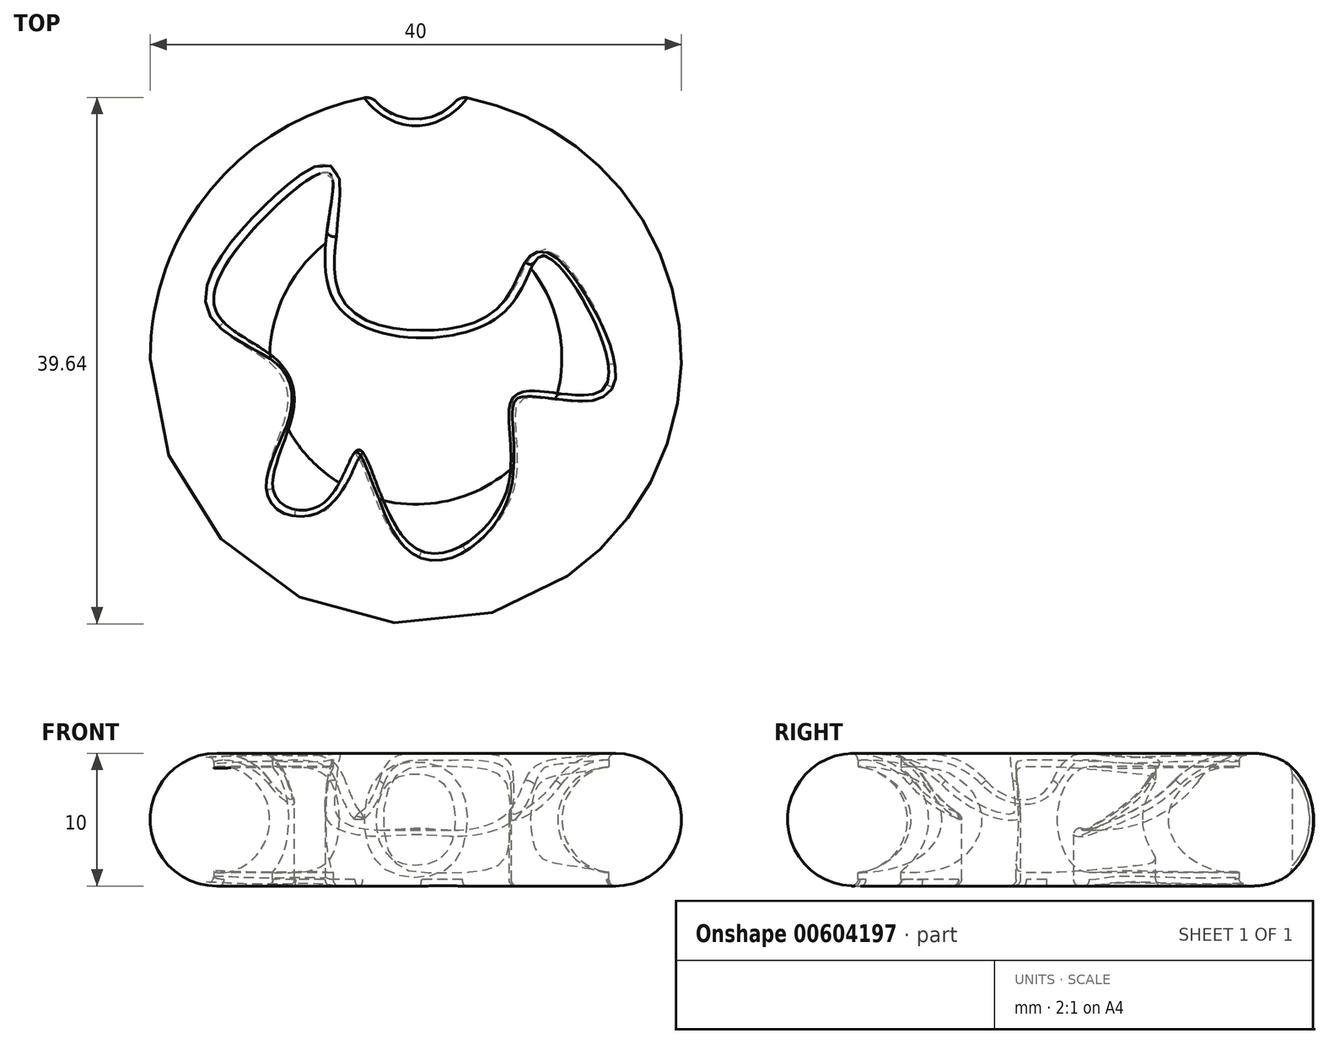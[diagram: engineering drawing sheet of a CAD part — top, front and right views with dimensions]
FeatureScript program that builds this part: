
annotation { "Feature Type Name" : "Feature", "Feature Type Description" : "" }
export const myFeature = defineFeature(function(context is Context, id is Id, definition is map)
    precondition{}
    {
        {
            var Q0;
            Q0=qCreatedBy(makeId("Front.planeOp"),FACE);
            var sketch = newSketch(context, id + "F0", { "sketchPlane" : qUnion([Q0])});
            skArc(sketch, "E0", {"start": v(-10.95, 7.94) * mm, "mid": v(-6, 4.53) * mm, "end": v(0, 5) * mm});
            skArc(sketch, "E1", {"start": v(-10.95, 7.94) * mm, "mid": v(-19.45, 7.27) * mm, "end": v(-15, 0) * mm});
            skLineSegment(sketch, "E2", {"start": v(-15, 0) * mm, "end": v(0, 0) * mm});
            skLineSegment(sketch, "E3", {"start": v(0, 0) * mm, "end": v(0, 5) * mm});
            skPoint(sketch, "E4.orphan", {"position": v(-17.04, 0) * mm});
            skSolve(sketch);
        }
        {
            var Q0;
            Q0=makeQuery(id+"F0.imprint","IMPRINT",FACE,{"disambiguationData":[TD([[makeQuery(id+"F0.imprint","IMPRINT",EDGE,{"derivedFrom":sQuery(id+"F0.wireOp",EDGE,"E0")}),-1.0]])]});
            var Q1;
            Q1=sQuery(id+"F0.wireOp",EDGE,"E3");
            revolve(context, id + "F1", {"entities" : qUnion([Q0]), "axis" : qUnion([Q1]), "revolveType" : RevolveType.FULL});
        }
        {
            var Q0;
            Q0=qCreatedBy(makeId("Top.planeOp"),FACE);
            cPlane(context, id + "F2", {"entities" : qUnion([Q0]), "cplaneType" : CPlaneType.OFFSET, "offset" : 10 * mm, "width" : 150 * mm, "height" : 150 * mm});
        }
        {
            var Q0;
            Q0=qCreatedBy(id+"F2.planeOp",FACE);
            var sketch = newSketch(context, id + "F3", { "sketchPlane" : qUnion([Q0])});
            skFitSpline(sketch, "E5", {"points": [v(-15.11, 3.71) * mm, v(-11.13, 10.87) * mm, v(-6.36, 13.79) * mm, v(-6.1, 4.24) * mm, v(6.63, 3.45) * mm, v(9.8, 7.69) * mm, v(14.32, -2.12) * mm, v(7.69, -2.65) * mm, v(6.9, -9.8) * mm, v(0, -14.32) * mm, v(-4.24, -6.9) * mm, v(-6.9, -10.87) * mm, v(-10.6, -10.34) * mm, v(-9.28, -4.24) * mm, v(-10.6, 0) * mm, v(-15.11, 3.71) * mm]});
            skSolve(sketch);
        }
        {
            var Q0;
            Q0=qSketchRegion(id+"F3",true);
            extrude(context, id + "F4", {"entities" : qUnion([Q0]), "operationType" : NewBodyOperationType.REMOVE, "endBound" : BoundingType.THROUGH_ALL, "oppositeDirection" : true, "depth" : 25 * mm});
        }
        {
            var Q0;
            Q0=qCreatedBy(makeId("Front.planeOp"),FACE);
            var sketch = newSketch(context, id + "F5", { "sketchPlane" : qUnion([Q0])});
            skCircle(sketch, "E6", {"center": v(-15, 5) * mm, "radius": 4 * mm});
            skSolve(sketch);
        }
        {
            var Q0;
            Q0=qSketchRegion(id+"F5",true);
            var Q1;
            Q1=sQuery(id+"F0.wireOp",EDGE,"E3");
            revolve(context, id + "F6", {"operationType" : NewBodyOperationType.ADD, "entities" : qUnion([Q0]), "axis" : qUnion([Q1]), "revolveType" : RevolveType.FULL});
        }
        {
            var Q0;
            Q0=qCreatedBy(makeId("Top.planeOp"),FACE);
            var sketch = newSketch(context, id + "F7", { "sketchPlane" : qUnion([Q0])});
            skCircle(sketch, "E7", {"center": v(0, 22) * mm, "radius": 4 * mm});
            skSolve(sketch);
        }
        {
            var Q0;
            Q0=makeQuery(id+"F7.imprint","IMPRINT",FACE,{"disambiguationData":[TD([[makeQuery(id+"F7.imprint","IMPRINT",EDGE,{"derivedFrom":sQuery(id+"F7.wireOp",EDGE,"E7")}),1.0]])]});
            extrude(context, id + "F8", {"entities" : qUnion([Q0]), "operationType" : NewBodyOperationType.REMOVE, "oppositeDirection" : true, "depth" : 25 * mm});
        }
        {
            var Q0;
            Q0=makeQuery(id+"F7.imprint","IMPRINT",FACE,{"disambiguationData":[TD([[makeQuery(id+"F7.imprint","IMPRINT",EDGE,{"derivedFrom":sQuery(id+"F7.wireOp",EDGE,"E7")}),1.0]])]});
            extrude(context, id + "F9", {"entities" : qUnion([Q0]), "operationType" : NewBodyOperationType.REMOVE, "oppositeDirection" : true, "depth" : 25 * mm});
        }
        {
            var Q0;
            Q0=makeQuery(id+"F7.imprint","IMPRINT",FACE,{"disambiguationData":[TD([[makeQuery(id+"F7.imprint","IMPRINT",EDGE,{"derivedFrom":sQuery(id+"F7.wireOp",EDGE,"E7")}),1.0]])]});
            extrude(context, id + "F10", {"entities" : qUnion([Q0]), "operationType" : NewBodyOperationType.REMOVE, "depth" : 34.3 * mm});
        }
        {
            var Q0;
            Q0=makeQuery(id+"F10.boolean.opBoolean","INTERSECT",EDGE,{"derivedFrom":[makeQuery(id+"F1.opRevolve","SWEPT_FACE",FACE,{"disambiguationData":[OSD([sQuery(id+"F0.wireOp",EDGE,"E1")])]}),makeQuery(id+"F10.opExtrude","SWEPT_FACE",FACE,{"disambiguationData":[OSD([sQuery(id+"F7.wireOp",EDGE,"E7")])]})]});
            fillet(context, id + "F11", {"entities" : qUnion([Q0]), "radius" : 1 * mm, "tangentPropagation" : true, "allowEdgeOverflow" : false});
        }
        {
            var Q0;
            Q0=makeQuery(id+"F4.boolean.opBoolean","INTERSECT",EDGE,{"derivedFrom":[makeQuery(id+"F1.opRevolve","SWEPT_FACE",FACE,{"disambiguationData":[OSD([sQuery(id+"F0.wireOp",EDGE,"E2")])]}),makeQuery(id+"F4.opExtrude","SWEPT_FACE",FACE,{"disambiguationData":[OSD([sQuery(id+"F3.wireOp",EDGE,"E5")])]})]});
            var Q1;
            Q1=makeQuery(id+"F4.boolean.opBoolean","INTERSECT",EDGE,{"disambiguationData":[OD(1.0)],"derivedFrom":[makeQuery(id+"F1.opRevolve","SWEPT_FACE",FACE,{"disambiguationData":[OSD([sQuery(id+"F0.wireOp",EDGE,"E1")])]}),makeQuery(id+"F4.opExtrude","SWEPT_FACE",FACE,{"disambiguationData":[OSD([sQuery(id+"F3.wireOp",EDGE,"E5")])]})]});
            fillet(context, id + "F12", {"entities" : qUnion([Q0, Q1]), "radius" : 0.5 * mm, "tangentPropagation" : true, "allowEdgeOverflow" : false});
        }
    });
